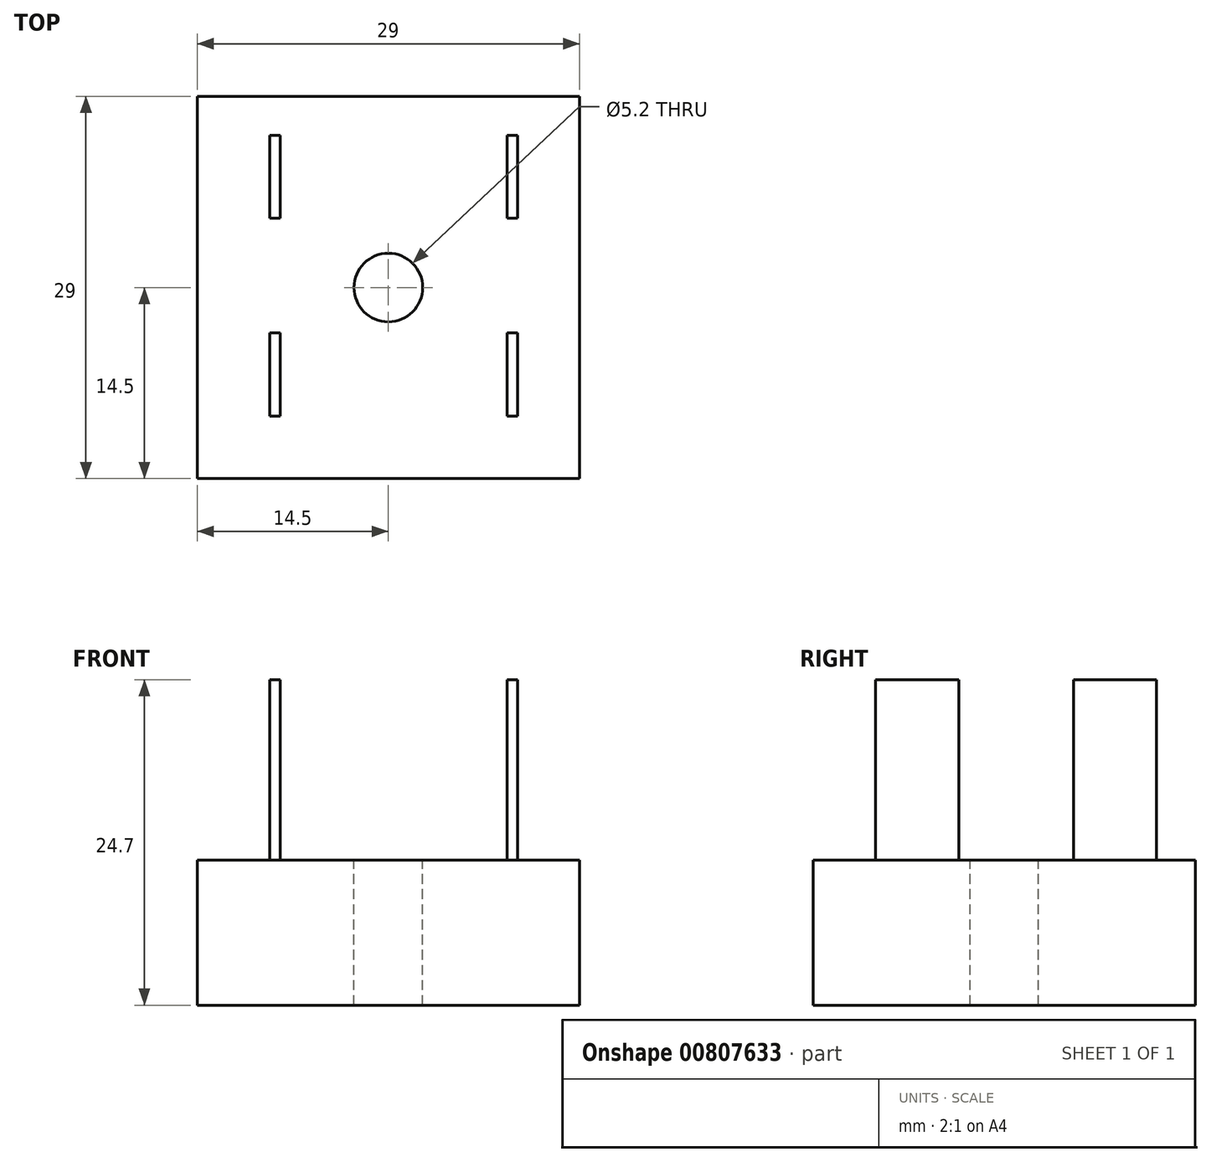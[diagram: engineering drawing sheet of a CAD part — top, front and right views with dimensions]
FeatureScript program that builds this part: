
annotation { "Feature Type Name" : "Feature", "Feature Type Description" : "" }
export const myFeature = defineFeature(function(context is Context, id is Id, definition is map)
    precondition{}
    {
        {
            var Q0;
            Q0=qCreatedBy(makeId("Top.planeOp"),FACE);
            var sketch = newSketch(context, id + "F0", { "sketchPlane" : qUnion([Q0])});
            skLineSegment(sketch, "E0.bottom", {"start": v(14.5, -14.5) * mm, "end": v(-14.5, -14.5) * mm});
            skLineSegment(sketch, "E0.top", {"start": v(14.5, 14.5) * mm, "end": v(-14.5, 14.5) * mm});
            skLineSegment(sketch, "E0.left", {"start": v(14.5, -14.5) * mm, "end": v(14.5, 14.5) * mm});
            skLineSegment(sketch, "E0.right", {"start": v(-14.5, -14.5) * mm, "end": v(-14.5, 14.5) * mm});
            skPoint(sketch, "E0.middle", {"position": v(0, 0) * mm});
            skSolve(sketch);
        }
        {
            var Q0;
            Q0 = qSketchRegion(id + "F0", true);
            extrude(context, id + "F1", {"entities" : qUnion([Q0]), "depth" : 11 * mm, "offsetDistance" : 25 * mm});
        }
        {
            var Q0;
            Q0=makeQuery(id+"F1.opExtrude","CAP_FACE",FACE,{"disambiguationData":[OSD([sQuery(id+"F0.wireOp",EDGE,"E0.bottom"),sQuery(id+"F0.wireOp",EDGE,"E0.top"),sQuery(id+"F0.wireOp",EDGE,"E0.left"),sQuery(id+"F0.wireOp",EDGE,"E0.right")])],"isStart":false});
            var sketch = newSketch(context, id + "F2", { "sketchPlane" : qUnion([Q0])});
            skCircle(sketch, "E1", {"center": v(0, 0) * mm, "radius": 2.6 * mm});
            skSolve(sketch);
        }
        {
            var Q0;
            Q0 = qSketchRegion(id + "F2", true);
            extrude(context, id + "F3", {"entities" : qUnion([Q0]), "operationType" : NewBodyOperationType.REMOVE, "endBound" : BoundingType.THROUGH_ALL, "oppositeDirection" : true, "depth" : 25 * mm, "offsetDistance" : 25 * mm});
        }
        {
            var Q0;
            Q0=makeQuery(id+"F1.opExtrude","CAP_FACE",FACE,{"disambiguationData":[OSD([sQuery(id+"F0.wireOp",EDGE,"E0.bottom"),sQuery(id+"F0.wireOp",EDGE,"E0.top"),sQuery(id+"F0.wireOp",EDGE,"E0.left"),sQuery(id+"F0.wireOp",EDGE,"E0.right")])],"isStart":false});
            var sketch = newSketch(context, id + "F4", { "sketchPlane" : qUnion([Q0])});
            skLineSegment(sketch, "E2.bottom", {"start": v(9.8, 5.25) * mm, "end": v(9, 5.25) * mm});
            skLineSegment(sketch, "E2.top", {"start": v(9.8, 11.55) * mm, "end": v(9, 11.55) * mm});
            skLineSegment(sketch, "E2.left", {"start": v(9.8, 5.25) * mm, "end": v(9.8, 11.55) * mm});
            skLineSegment(sketch, "E2.right", {"start": v(9, 5.25) * mm, "end": v(9, 11.55) * mm});
            skPoint(sketch, "E2.middle", {"position": v(9.4, 8.4) * mm});
            skLineSegment(sketch, "E3.0.1.0", {"start": v(9, -9.75) * mm, "end": v(9, -3.45) * mm});
            skLineSegment(sketch, "E3.0.1.1", {"start": v(9.8, -9.75) * mm, "end": v(9.8, -3.45) * mm});
            skPoint(sketch, "E3.0.1.2", {"position": v(9.4, -6.6) * mm});
            skLineSegment(sketch, "E3.0.1.3", {"start": v(9.8, -3.45) * mm, "end": v(9, -3.45) * mm});
            skLineSegment(sketch, "E3.0.1.4", {"start": v(9.8, -9.75) * mm, "end": v(9, -9.75) * mm});
            skLineSegment(sketch, "E3.1.0.0", {"start": v(-9, 5.25) * mm, "end": v(-9, 11.55) * mm});
            skLineSegment(sketch, "E3.1.0.1", {"start": v(-8.2, 5.25) * mm, "end": v(-8.2, 11.55) * mm});
            skPoint(sketch, "E3.1.0.2", {"position": v(-8.6, 8.4) * mm});
            skLineSegment(sketch, "E3.1.0.3", {"start": v(-8.2, 11.55) * mm, "end": v(-9, 11.55) * mm});
            skLineSegment(sketch, "E3.1.0.4", {"start": v(-8.2, 5.25) * mm, "end": v(-9, 5.25) * mm});
            skLineSegment(sketch, "E3.1.1.0", {"start": v(-9, -9.75) * mm, "end": v(-9, -3.45) * mm});
            skLineSegment(sketch, "E3.1.1.1", {"start": v(-8.2, -9.75) * mm, "end": v(-8.2, -3.45) * mm});
            skPoint(sketch, "E3.1.1.2", {"position": v(-8.6, -6.6) * mm});
            skLineSegment(sketch, "E3.1.1.3", {"start": v(-8.2, -3.45) * mm, "end": v(-9, -3.45) * mm});
            skLineSegment(sketch, "E3.1.1.4", {"start": v(-8.2, -9.75) * mm, "end": v(-9, -9.75) * mm});
            skLineSegment(sketch, "E3.direction1", {"start": v(9, 5.25) * mm, "end": v(-9, 5.25) * mm, "construction": true});
            skLineSegment(sketch, "E3.direction2", {"start": v(9, 5.25) * mm, "end": v(9, -9.75) * mm, "construction": true});
            skSolve(sketch);
        }
        {
            var Q0;
            Q0 = qSketchRegion(id + "F4", true);
            extrude(context, id + "F5", {"entities" : qUnion([Q0]), "operationType" : NewBodyOperationType.ADD, "depth" : (21.7 - 8) * mm, "offsetDistance" : 25 * mm});
        }
    });
